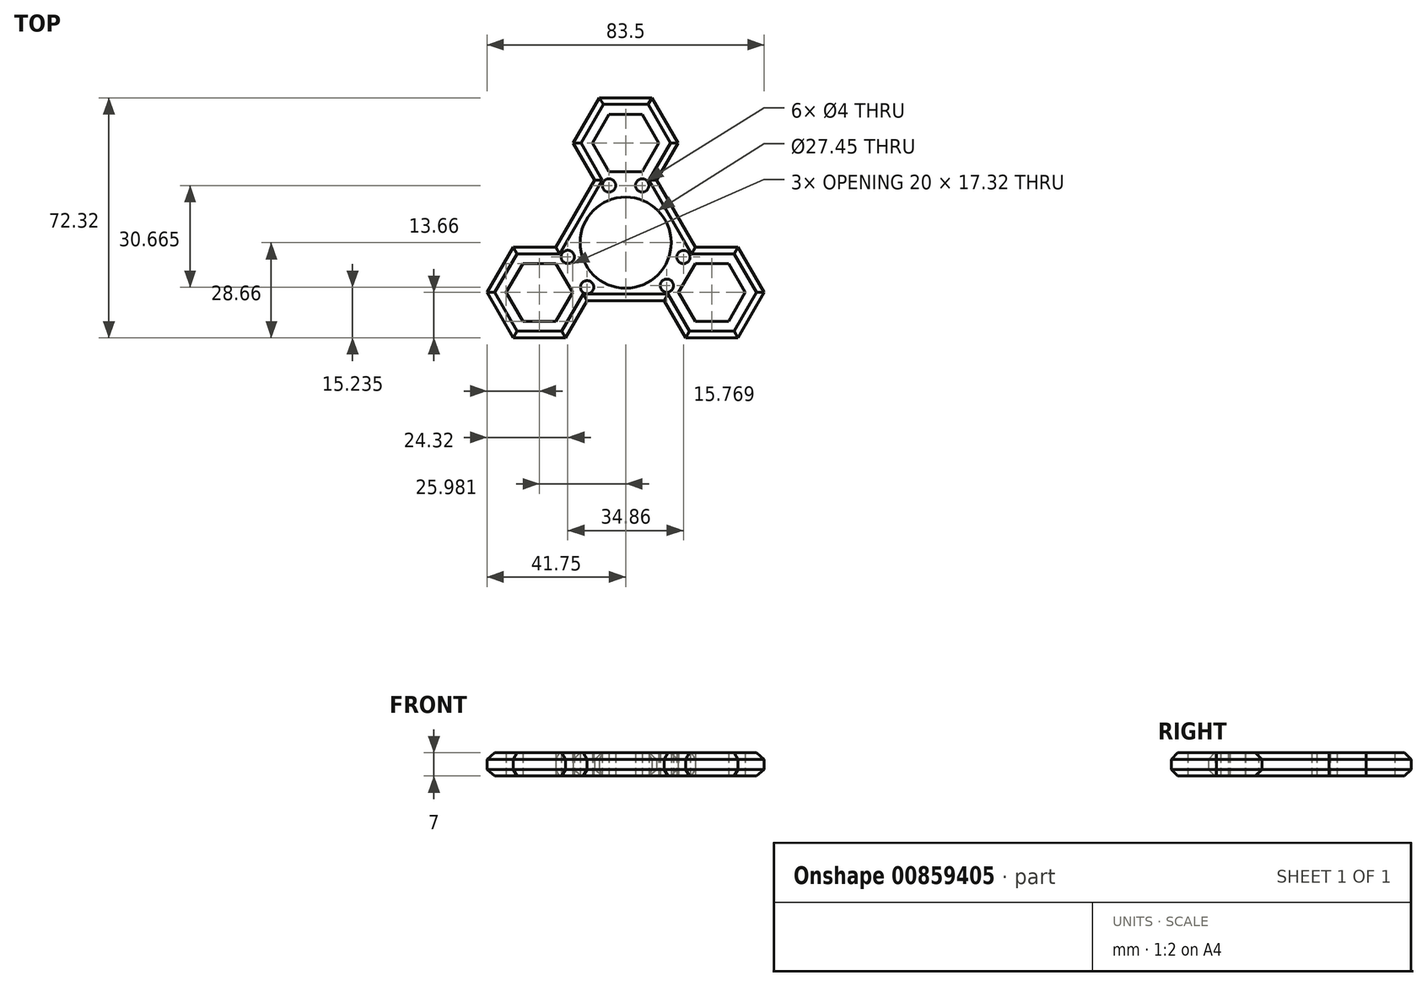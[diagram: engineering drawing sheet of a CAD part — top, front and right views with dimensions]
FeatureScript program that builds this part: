
annotation { "Feature Type Name" : "Feature", "Feature Type Description" : "" }
export const myFeature = defineFeature(function(context is Context, id is Id, definition is map)
    precondition{}
    {
        {
            var Q0;
            Q0=qCreatedBy(makeId("Top.planeOp"),FACE);
            var sketch = newSketch(context, id + "F0", { "sketchPlane" : qUnion([Q0])});
            skCircle(sketch, "E0", {"center": v(0, 0) * mm, "radius": 13.73 * mm});
            skCircle(sketch, "E1.cCircle", {"center": v(-25.98, -15) * mm, "radius": 8.66 * mm, "construction": true});
            skLineSegment(sketch, "E1.0", {"start": v(-20.98, -6.34) * mm, "end": v(-15.98, -15) * mm});
            skLineSegment(sketch, "E1.1", {"start": v(-15.98, -15) * mm, "end": v(-20.98, -23.66) * mm});
            skLineSegment(sketch, "E1.2", {"start": v(-20.98, -23.66) * mm, "end": v(-30.98, -23.66) * mm});
            skLineSegment(sketch, "E1.3", {"start": v(-30.98, -23.66) * mm, "end": v(-35.98, -15) * mm});
            skLineSegment(sketch, "E1.4", {"start": v(-35.98, -15) * mm, "end": v(-30.98, -6.34) * mm});
            skLineSegment(sketch, "E1.5", {"start": v(-30.98, -6.34) * mm, "end": v(-20.98, -6.34) * mm});
            skCircle(sketch, "E2.cCircle", {"center": v(25.98, -15) * mm, "radius": 8.66 * mm, "construction": true});
            skLineSegment(sketch, "E2.0", {"start": v(15.98, -15) * mm, "end": v(20.98, -6.34) * mm});
            skLineSegment(sketch, "E2.1", {"start": v(20.98, -6.34) * mm, "end": v(30.98, -6.34) * mm});
            skLineSegment(sketch, "E2.2", {"start": v(30.98, -6.34) * mm, "end": v(35.98, -15) * mm});
            skLineSegment(sketch, "E2.3", {"start": v(35.98, -15) * mm, "end": v(30.98, -23.66) * mm});
            skLineSegment(sketch, "E2.4", {"start": v(30.98, -23.66) * mm, "end": v(20.98, -23.66) * mm});
            skLineSegment(sketch, "E2.5", {"start": v(20.98, -23.66) * mm, "end": v(15.98, -15) * mm});
            skCircle(sketch, "E3.cCircle", {"center": v(0, 30) * mm, "radius": 8.66 * mm, "construction": true});
            skLineSegment(sketch, "E3.0", {"start": v(5, 21.34) * mm, "end": v(-5, 21.34) * mm});
            skLineSegment(sketch, "E3.1", {"start": v(-5, 21.34) * mm, "end": v(-10, 30) * mm});
            skLineSegment(sketch, "E3.2", {"start": v(-10, 30) * mm, "end": v(-5, 38.66) * mm});
            skLineSegment(sketch, "E3.3", {"start": v(-5, 38.66) * mm, "end": v(5, 38.66) * mm});
            skLineSegment(sketch, "E3.4", {"start": v(5, 38.66) * mm, "end": v(10, 30) * mm});
            skLineSegment(sketch, "E3.5", {"start": v(10, 30) * mm, "end": v(5, 21.34) * mm});
            skLineSegment(sketch, "E4.0", {"start": v(-5, 43.66) * mm, "end": v(5, 43.66) * mm});
            skLineSegment(sketch, "E5.0", {"start": v(-14.33, 32.5) * mm, "end": v(-9.33, 41.16) * mm});
            skLineSegment(sketch, "E6.0", {"start": v(9.33, 41.16) * mm, "end": v(14.33, 32.5) * mm});
            skLineSegment(sketch, "E7.0", {"start": v(-9.33, 18.84) * mm, "end": v(-14.33, 27.5) * mm});
            skLineSegment(sketch, "E8.0", {"start": v(14.33, 27.5) * mm, "end": v(9.33, 18.84) * mm});
            skLineSegment(sketch, "E9.0", {"start": v(-30.98, -1.34) * mm, "end": v(-20.98, -1.34) * mm});
            skLineSegment(sketch, "E10.0", {"start": v(-40.31, -12.5) * mm, "end": v(-35.31, -3.84) * mm});
            skLineSegment(sketch, "E11.0", {"start": v(-35.31, -26.16) * mm, "end": v(-40.31, -17.5) * mm});
            skLineSegment(sketch, "E12.0", {"start": v(-20.98, -28.66) * mm, "end": v(-30.98, -28.66) * mm});
            skLineSegment(sketch, "E13.0", {"start": v(-11.65, -17.5) * mm, "end": v(-16.65, -26.16) * mm});
            skLineSegment(sketch, "E14.0", {"start": v(16.65, -26.16) * mm, "end": v(11.65, -17.5) * mm});
            skLineSegment(sketch, "E15.0", {"start": v(30.98, -28.66) * mm, "end": v(20.98, -28.66) * mm});
            skLineSegment(sketch, "E16.0", {"start": v(40.3, -17.5) * mm, "end": v(35.31, -26.16) * mm});
            skLineSegment(sketch, "E17.0", {"start": v(35.31, -3.84) * mm, "end": v(40.31, -12.5) * mm});
            skLineSegment(sketch, "E18.0", {"start": v(20.98, -1.34) * mm, "end": v(30.98, -1.34) * mm});
            skLineSegment(sketch, "E19", {"start": v(14.33, 27.5) * mm, "end": v(15.77, 30) * mm});
            skLineSegment(sketch, "E20", {"start": v(14.33, 32.5) * mm, "end": v(15.77, 30) * mm});
            skLineSegment(sketch, "E21", {"start": v(-14.33, 27.5) * mm, "end": v(-15.77, 30) * mm});
            skLineSegment(sketch, "E22", {"start": v(-14.33, 32.5) * mm, "end": v(-15.77, 30) * mm});
            skLineSegment(sketch, "E23", {"start": v(-5, 43.66) * mm, "end": v(-7.89, 43.66) * mm});
            skLineSegment(sketch, "E24", {"start": v(5, 43.66) * mm, "end": v(7.89, 43.66) * mm});
            skLineSegment(sketch, "E25", {"start": v(-9.33, 41.16) * mm, "end": v(-7.89, 43.66) * mm});
            skLineSegment(sketch, "E26", {"start": v(9.33, 41.16) * mm, "end": v(7.89, 43.66) * mm});
            skLineSegment(sketch, "E27", {"start": v(30.98, -1.34) * mm, "end": v(33.87, -1.34) * mm});
            skLineSegment(sketch, "E28", {"start": v(35.31, -3.84) * mm, "end": v(33.87, -1.34) * mm});
            skLineSegment(sketch, "E29", {"start": v(40.31, -12.5) * mm, "end": v(41.75, -15) * mm});
            skLineSegment(sketch, "E30", {"start": v(40.3, -17.5) * mm, "end": v(41.75, -15) * mm});
            skLineSegment(sketch, "E31", {"start": v(35.31, -26.16) * mm, "end": v(33.87, -28.66) * mm});
            skLineSegment(sketch, "E32", {"start": v(16.65, -26.16) * mm, "end": v(18.1, -28.66) * mm});
            skLineSegment(sketch, "E33", {"start": v(30.98, -28.66) * mm, "end": v(33.87, -28.66) * mm});
            skLineSegment(sketch, "E34", {"start": v(20.98, -28.66) * mm, "end": v(18.1, -28.66) * mm});
            skLineSegment(sketch, "E35", {"start": v(-30.98, -1.34) * mm, "end": v(-33.87, -1.34) * mm});
            skLineSegment(sketch, "E36", {"start": v(-35.31, -3.84) * mm, "end": v(-33.87, -1.34) * mm});
            skLineSegment(sketch, "E37", {"start": v(-40.31, -12.5) * mm, "end": v(-41.75, -15) * mm});
            skLineSegment(sketch, "E38", {"start": v(-40.31, -17.5) * mm, "end": v(-41.75, -15) * mm});
            skLineSegment(sketch, "E39", {"start": v(-35.31, -26.16) * mm, "end": v(-33.87, -28.66) * mm});
            skLineSegment(sketch, "E40", {"start": v(-30.98, -28.66) * mm, "end": v(-33.87, -28.66) * mm});
            skLineSegment(sketch, "E41", {"start": v(-20.98, -28.66) * mm, "end": v(-18.1, -28.66) * mm});
            skLineSegment(sketch, "E42", {"start": v(-16.65, -26.16) * mm, "end": v(-18.1, -28.66) * mm});
            skLineSegment(sketch, "E43", {"start": v(-20.98, -1.34) * mm, "end": v(-9.33, 18.84) * mm});
            skLineSegment(sketch, "E44", {"start": v(9.33, 18.84) * mm, "end": v(20.98, -1.34) * mm});
            skLineSegment(sketch, "E45", {"start": v(-11.65, -17.5) * mm, "end": v(11.65, -17.5) * mm});
            skCircle(sketch, "E46", {"center": v(-5, 17.24) * mm, "radius": 2 * mm});
            skCircle(sketch, "E47", {"center": v(5, 17.24) * mm, "radius": 2 * mm});
            skCircle(sketch, "E48", {"center": v(-17.43, -4.29) * mm, "radius": 2 * mm});
            skCircle(sketch, "E49", {"center": v(-11.6, -13.42) * mm, "radius": 2 * mm});
            skCircle(sketch, "E50", {"center": v(12.43, -12.95) * mm, "radius": 2 * mm});
            skCircle(sketch, "E51", {"center": v(17.43, -4.34) * mm, "radius": 2 * mm});
            skSolve(sketch);
        }
        {
            var Q0;
            Q0=makeQuery(id+"F0.imprint","IMPRINT",FACE,{"disambiguationData":[TD([[makeQuery(id+"F0.imprint","IMPRINT",EDGE,{"derivedFrom":sQuery(id+"F0.wireOp",EDGE,"E0")}),-1.0]])]});
            extrude(context, id + "F1", {"entities" : qUnion([Q0]), "depth" : 7 * mm, "offsetDistance" : 25 * mm});
        }
        {
            var Q0;
            Q0=makeQuery(id+"F1.opExtrude","CAP_EDGE",EDGE,{"disambiguationData":[OSD([sQuery(id+"F0.wireOp",EDGE,"E5.0"),sQuery(id+"F0.wireOp",EDGE,"E22"),sQuery(id+"F0.wireOp",EDGE,"E25")])],"isStart":false});
            var Q1;
            Q1=makeQuery(id+"F1.opExtrude","CAP_EDGE",EDGE,{"disambiguationData":[OSD([sQuery(id+"F0.wireOp",EDGE,"E4.0"),sQuery(id+"F0.wireOp",EDGE,"E23"),sQuery(id+"F0.wireOp",EDGE,"E24")])],"isStart":false});
            var Q2;
            Q2=makeQuery(id+"F1.opExtrude","CAP_EDGE",EDGE,{"disambiguationData":[OSD([sQuery(id+"F0.wireOp",EDGE,"E7.0"),sQuery(id+"F0.wireOp",EDGE,"E21")])],"isStart":false});
            var Q3;
            Q3=makeQuery(id+"F1.opExtrude","CAP_EDGE",EDGE,{"disambiguationData":[OSD([sQuery(id+"F0.wireOp",EDGE,"E6.0"),sQuery(id+"F0.wireOp",EDGE,"E20"),sQuery(id+"F0.wireOp",EDGE,"E26")])],"isStart":false});
            var Q4;
            Q4=makeQuery(id+"F1.opExtrude","CAP_EDGE",EDGE,{"disambiguationData":[OSD([sQuery(id+"F0.wireOp",EDGE,"E8.0"),sQuery(id+"F0.wireOp",EDGE,"E19")])],"isStart":false});
            var Q5;
            Q5=makeQuery(id+"F1.opExtrude","CAP_EDGE",EDGE,{"disambiguationData":[OSD([sQuery(id+"F0.wireOp",EDGE,"E44")])],"isStart":false});
            var Q6;
            Q6=makeQuery(id+"F1.opExtrude","CAP_EDGE",EDGE,{"disambiguationData":[OSD([sQuery(id+"F0.wireOp",EDGE,"E18.0"),sQuery(id+"F0.wireOp",EDGE,"E27")])],"isStart":false});
            var Q7;
            Q7=makeQuery(id+"F1.opExtrude","CAP_EDGE",EDGE,{"disambiguationData":[OSD([sQuery(id+"F0.wireOp",EDGE,"E17.0"),sQuery(id+"F0.wireOp",EDGE,"E28"),sQuery(id+"F0.wireOp",EDGE,"E29")])],"isStart":false});
            var Q8;
            Q8=makeQuery(id+"F1.opExtrude","CAP_EDGE",EDGE,{"disambiguationData":[OSD([sQuery(id+"F0.wireOp",EDGE,"E16.0"),sQuery(id+"F0.wireOp",EDGE,"E30"),sQuery(id+"F0.wireOp",EDGE,"E31")])],"isStart":false});
            var Q9;
            Q9=makeQuery(id+"F1.opExtrude","CAP_EDGE",EDGE,{"disambiguationData":[OSD([sQuery(id+"F0.wireOp",EDGE,"E15.0"),sQuery(id+"F0.wireOp",EDGE,"E33"),sQuery(id+"F0.wireOp",EDGE,"E34")])],"isStart":false});
            var Q10;
            Q10=makeQuery(id+"F1.opExtrude","CAP_EDGE",EDGE,{"disambiguationData":[OSD([sQuery(id+"F0.wireOp",EDGE,"E14.0"),sQuery(id+"F0.wireOp",EDGE,"E32")])],"isStart":false});
            var Q11;
            Q11=makeQuery(id+"F1.opExtrude","CAP_EDGE",EDGE,{"disambiguationData":[OSD([sQuery(id+"F0.wireOp",EDGE,"E45")])],"isStart":false});
            var Q12;
            Q12=makeQuery(id+"F1.opExtrude","CAP_EDGE",EDGE,{"disambiguationData":[OSD([sQuery(id+"F0.wireOp",EDGE,"E13.0"),sQuery(id+"F0.wireOp",EDGE,"E42")])],"isStart":false});
            var Q13;
            Q13=makeQuery(id+"F1.opExtrude","CAP_EDGE",EDGE,{"disambiguationData":[OSD([sQuery(id+"F0.wireOp",EDGE,"E12.0"),sQuery(id+"F0.wireOp",EDGE,"E40"),sQuery(id+"F0.wireOp",EDGE,"E41")])],"isStart":false});
            var Q14;
            Q14=makeQuery(id+"F1.opExtrude","CAP_EDGE",EDGE,{"disambiguationData":[OSD([sQuery(id+"F0.wireOp",EDGE,"E11.0"),sQuery(id+"F0.wireOp",EDGE,"E38"),sQuery(id+"F0.wireOp",EDGE,"E39")])],"isStart":false});
            var Q15;
            Q15=makeQuery(id+"F1.opExtrude","CAP_EDGE",EDGE,{"disambiguationData":[OSD([sQuery(id+"F0.wireOp",EDGE,"E10.0"),sQuery(id+"F0.wireOp",EDGE,"E36"),sQuery(id+"F0.wireOp",EDGE,"E37")])],"isStart":false});
            var Q16;
            Q16=makeQuery(id+"F1.opExtrude","CAP_EDGE",EDGE,{"disambiguationData":[OSD([sQuery(id+"F0.wireOp",EDGE,"E9.0"),sQuery(id+"F0.wireOp",EDGE,"E35")])],"isStart":false});
            var Q17;
            Q17=makeQuery(id+"F1.opExtrude","CAP_EDGE",EDGE,{"disambiguationData":[OSD([sQuery(id+"F0.wireOp",EDGE,"E43")])],"isStart":false});
            var Q18;
            Q18=makeQuery(id+"F1.opExtrude","CAP_EDGE",EDGE,{"disambiguationData":[OSD([sQuery(id+"F0.wireOp",EDGE,"E9.0"),sQuery(id+"F0.wireOp",EDGE,"E35")])],"isStart":true});
            var Q19;
            Q19=makeQuery(id+"F1.opExtrude","CAP_EDGE",EDGE,{"disambiguationData":[OSD([sQuery(id+"F0.wireOp",EDGE,"E10.0"),sQuery(id+"F0.wireOp",EDGE,"E36"),sQuery(id+"F0.wireOp",EDGE,"E37")])],"isStart":true});
            var Q20;
            Q20=makeQuery(id+"F1.opExtrude","CAP_EDGE",EDGE,{"disambiguationData":[OSD([sQuery(id+"F0.wireOp",EDGE,"E11.0"),sQuery(id+"F0.wireOp",EDGE,"E38"),sQuery(id+"F0.wireOp",EDGE,"E39")])],"isStart":true});
            var Q21;
            Q21=makeQuery(id+"F1.opExtrude","CAP_EDGE",EDGE,{"disambiguationData":[OSD([sQuery(id+"F0.wireOp",EDGE,"E12.0"),sQuery(id+"F0.wireOp",EDGE,"E40"),sQuery(id+"F0.wireOp",EDGE,"E41")])],"isStart":true});
            var Q22;
            Q22=makeQuery(id+"F1.opExtrude","CAP_EDGE",EDGE,{"disambiguationData":[OSD([sQuery(id+"F0.wireOp",EDGE,"E13.0"),sQuery(id+"F0.wireOp",EDGE,"E42")])],"isStart":true});
            var Q23;
            Q23=makeQuery(id+"F1.opExtrude","CAP_EDGE",EDGE,{"disambiguationData":[OSD([sQuery(id+"F0.wireOp",EDGE,"E45")])],"isStart":true});
            var Q24;
            Q24=makeQuery(id+"F1.opExtrude","CAP_EDGE",EDGE,{"disambiguationData":[OSD([sQuery(id+"F0.wireOp",EDGE,"E14.0"),sQuery(id+"F0.wireOp",EDGE,"E32")])],"isStart":true});
            var Q25;
            Q25=makeQuery(id+"F1.opExtrude","CAP_EDGE",EDGE,{"disambiguationData":[OSD([sQuery(id+"F0.wireOp",EDGE,"E15.0"),sQuery(id+"F0.wireOp",EDGE,"E33"),sQuery(id+"F0.wireOp",EDGE,"E34")])],"isStart":true});
            var Q26;
            Q26=makeQuery(id+"F1.opExtrude","CAP_EDGE",EDGE,{"disambiguationData":[OSD([sQuery(id+"F0.wireOp",EDGE,"E16.0"),sQuery(id+"F0.wireOp",EDGE,"E30"),sQuery(id+"F0.wireOp",EDGE,"E31")])],"isStart":true});
            var Q27;
            Q27=makeQuery(id+"F1.opExtrude","CAP_EDGE",EDGE,{"disambiguationData":[OSD([sQuery(id+"F0.wireOp",EDGE,"E17.0"),sQuery(id+"F0.wireOp",EDGE,"E28"),sQuery(id+"F0.wireOp",EDGE,"E29")])],"isStart":true});
            var Q28;
            Q28=makeQuery(id+"F1.opExtrude","CAP_EDGE",EDGE,{"disambiguationData":[OSD([sQuery(id+"F0.wireOp",EDGE,"E18.0"),sQuery(id+"F0.wireOp",EDGE,"E27")])],"isStart":true});
            var Q29;
            Q29=makeQuery(id+"F1.opExtrude","CAP_EDGE",EDGE,{"disambiguationData":[OSD([sQuery(id+"F0.wireOp",EDGE,"E44")])],"isStart":true});
            var Q30;
            Q30=makeQuery(id+"F1.opExtrude","CAP_EDGE",EDGE,{"disambiguationData":[OSD([sQuery(id+"F0.wireOp",EDGE,"E8.0"),sQuery(id+"F0.wireOp",EDGE,"E19")])],"isStart":true});
            var Q31;
            Q31=makeQuery(id+"F1.opExtrude","CAP_EDGE",EDGE,{"disambiguationData":[OSD([sQuery(id+"F0.wireOp",EDGE,"E6.0"),sQuery(id+"F0.wireOp",EDGE,"E20"),sQuery(id+"F0.wireOp",EDGE,"E26")])],"isStart":true});
            var Q32;
            Q32=makeQuery(id+"F1.opExtrude","CAP_EDGE",EDGE,{"disambiguationData":[OSD([sQuery(id+"F0.wireOp",EDGE,"E4.0"),sQuery(id+"F0.wireOp",EDGE,"E23"),sQuery(id+"F0.wireOp",EDGE,"E24")])],"isStart":true});
            var Q33;
            Q33=makeQuery(id+"F1.opExtrude","CAP_EDGE",EDGE,{"disambiguationData":[OSD([sQuery(id+"F0.wireOp",EDGE,"E5.0"),sQuery(id+"F0.wireOp",EDGE,"E22"),sQuery(id+"F0.wireOp",EDGE,"E25")])],"isStart":true});
            var Q34;
            Q34=makeQuery(id+"F1.opExtrude","CAP_EDGE",EDGE,{"disambiguationData":[OSD([sQuery(id+"F0.wireOp",EDGE,"E7.0"),sQuery(id+"F0.wireOp",EDGE,"E21")])],"isStart":true});
            var Q35;
            Q35=makeQuery(id+"F1.opExtrude","CAP_EDGE",EDGE,{"disambiguationData":[OSD([sQuery(id+"F0.wireOp",EDGE,"E43")])],"isStart":true});
            chamfer(context, id + "F2", {"entities" : qUnion([Q0, Q1, Q2, Q3, Q4, Q5, Q6, Q7, Q8, Q9, Q10, Q11, Q12, Q13, Q14, Q15, Q16, Q17, Q18, Q19, Q20, Q21, Q22, Q23, Q24, Q25, Q26, Q27, Q28, Q29, Q30, Q31, Q32, Q33, Q34, Q35]), "width" : 2 * mm, "tangentPropagation" : true});
        }
    });
